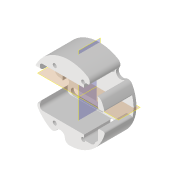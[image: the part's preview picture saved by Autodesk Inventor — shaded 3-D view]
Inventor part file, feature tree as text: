
AUTODESK INVENTOR PART (.ipt)
format: ipt  version: 2022 (Build 260153000, 153)  size: 313,344 bytes
history: native  units: in
note: dims shown in document units (in); Inventor stores cm internally (conversion verified against a paired STEP export)
features: other x8, sketch x8, extrude x7, fillet x5, reference x4, projected_geometry x3, plane x2, hole x1
ambient origin geometry x8: Origin, YZ Plane, XZ Plane, XY Plane, X Axis, Y Axis, Z Axis, Center Point
bodies: Solid2 (feature_tree)
feature tree (38):
  extrude  "Extrusion5"  Depth=0.0787in TaperAngle=0.0deg
  extrude  "Extrusion6"  Depth=0.7677in
  fillet  "Fillet2"  Radius=0.7677in
  extrude  "Extrusion7"  Depth=0.0787in TaperAngle=0.0deg
  hole  "Hole2"  [1 undecoded]
  plane  "Work Plane4"
  plane  "Work Plane5"
  fillet  "Fillet4"  Radius=0.0394in
  other  "Work Axis1"
  extrude  "Extrusion8"  Depth=0.6299in
  fillet  "Fillet5"  Radius=0.6299in
  extrude  "Extrusion9"  Depth=1.0in TaperAngle=0.0deg
  extrude  "Extrusion10"  Depth=0.125in
  fillet  "Fillet6"  Radius=0.2559in
  extrude  "Extrusion11"  Depth=0.125in
  fillet  "Fillet7"  Radius=0.2559in
  sketch  "Sketch6"  dims[d33=2.0472in d34=0.0787in d35=0.0in]
  sketch  "Sketch7"  dims[d36=1.6142in d37=1.122in d38=0.7677in d39=0.0in]
  sketch  "Sketch8"  dims[d40=0.0787in d41=0.4724in d42=0.0in]
  projected_geometry  "Projected Loop5"
  sketch  "Sketch9"  dims[d44=0.7874in d45=1.378in]
  projected_geometry  "Projected Loop6"
  sketch  "Sketch11"  dims[d46=0.1102in d47=0.75in d48=0.2559in d49=0.1181in d50=0.5635in d51=1.0in d52=0.8108in d53=0.0394in]
  projected_geometry  "Projected Loop7"
  sketch  "Sketch12"  dims[d57=0.0in d58=0.0in d59=0.7087in d60=0.6299in]
  reference  "Reference5"
  reference  "Reference6"
  reference  "Reference7"
  reference  "Reference8"
  sketch  "Sketch13"  dims[d61=0.1181in d62=1.0in d63=0.0in]
  sketch  "Sketch14"  dims[d64=1.0in d65=0.0in d66=0.1181in d67=0.2559in d68=0.2559in d69=0.2559in d70=1.0in d71=0.0in d72=0.125in]
  other  "<userpath>\Documents\MANATEE\INVENTOR\MANATEE_V1.iam"
  other  "MANATEE_V1.iam"
  other  "00_ESP3-CAM:1"
  other  "Pin Header 4 x 1 TH 2.54mm Pitch v1:1"
  other  "Pin Header 4 x 1 TH 2.54mm Pitch v1:2"
  other  "Pin Header 4 x 1 TH 2.54mm Pitch v1:3"
  other  "Pin Header 4 x 1 TH 2.54mm Pitch v1:4"
note: 1 required parameter value undecoded (feature->parameter linkage not recoverable at this tier; creation-order binding heuristic only, values carry confidence <= 0.55)
